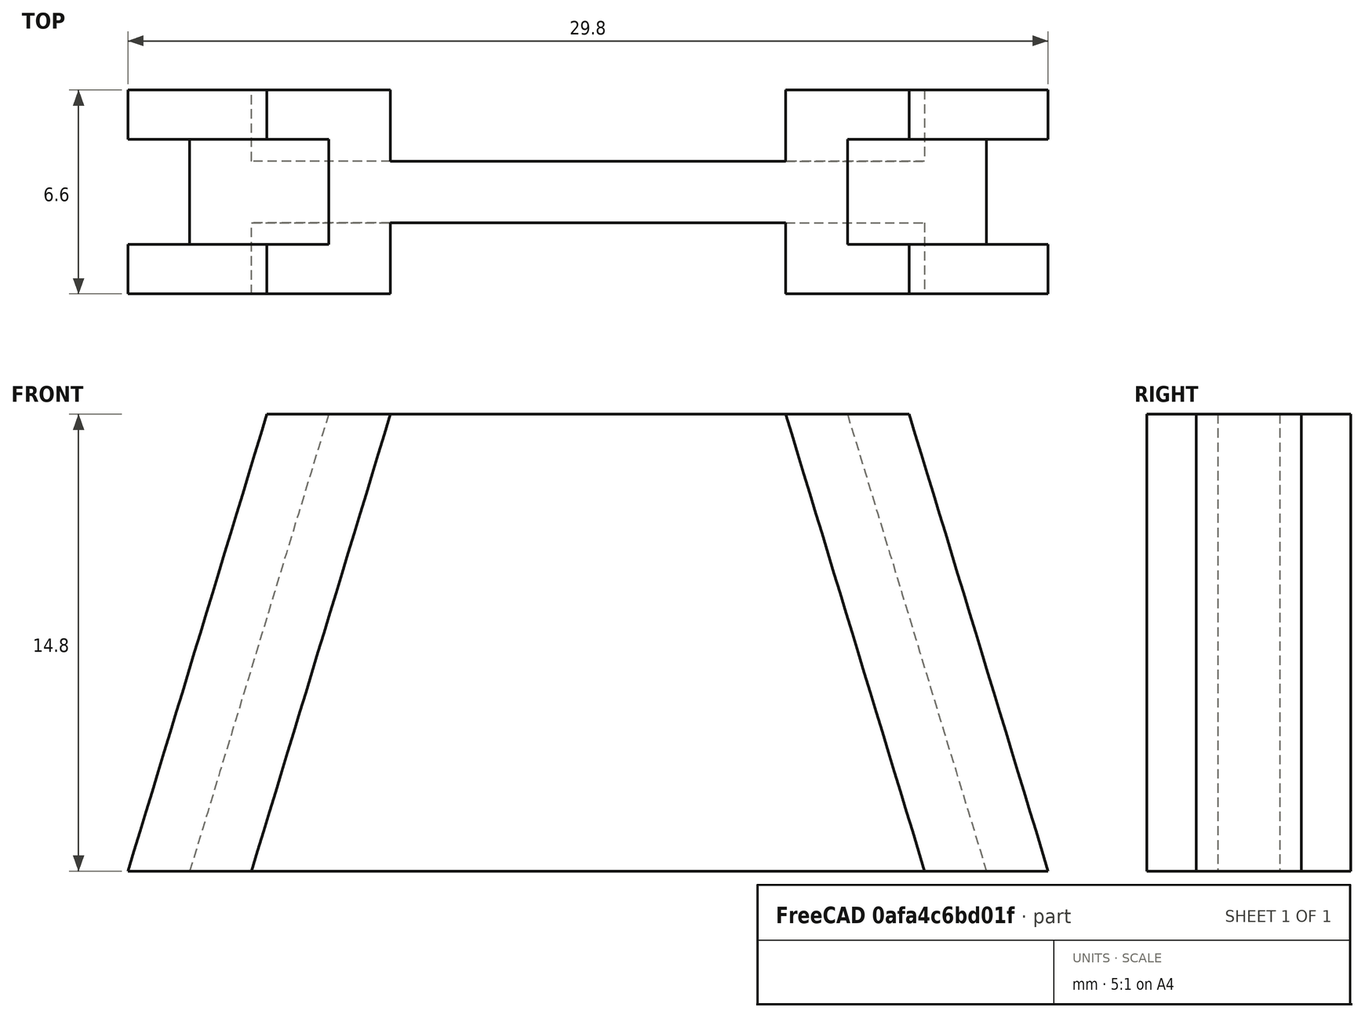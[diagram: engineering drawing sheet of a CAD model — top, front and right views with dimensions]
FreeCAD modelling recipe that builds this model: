
FCSTD DOCUMENT  (FreeCAD 0.18R4 (GitTag))
Label: smars_chassis_blank_v2
License: All rights reserved
LicenseURL: http://en.wikipedia.org/wiki/All_rights_reserved
objects: Sketcher::SketchObject×2, Part::Plane×1, PartDesign::AdditiveLoft×1, PartDesign::Body×1
note: 6 computed .brp shape members not serialized (recipe doc carries the construction recipe); baked Part::Feature solids carry a one-line shape summary decoded from their .brp

FEATURE [Part::Plane] Plane
  AttacherType = Attacher::AttachEngine3D
  Length = 10
  Placement = pos=(0,0,12.5) rot=(0,0,1;0rad)
  Width = 10
FEATURE [Sketcher::SketchObject] Sketch001  label="top"
  Support = -> [Plane]
  sketch-geometry (20):
    g0: LineSegment StartX=-14.9 StartY=-3.3 StartZ=0 EndX=-10.9 EndY=-3.3 EndZ=0
    g1: LineSegment StartX=-10.9 StartY=-3.3 StartZ=0 EndX=-10.9 EndY=-1 EndZ=0
    g2: LineSegment StartX=-10.9 StartY=-1 StartZ=0 EndX=10.9 EndY=-1 EndZ=0
    g3: LineSegment StartX=10.9 StartY=-1 StartZ=0 EndX=10.9 EndY=-3.3 EndZ=0
    g4: LineSegment StartX=10.9 StartY=-3.3 StartZ=0 EndX=14.9 EndY=-3.3 EndZ=0
    g5: LineSegment StartX=14.9 StartY=-3.3 StartZ=0 EndX=14.9 EndY=-1.7 EndZ=0
    g6: LineSegment StartX=14.9 StartY=-1.7 StartZ=0 EndX=12.9 EndY=-1.7 EndZ=0
    g7: LineSegment StartX=12.9 StartY=-1.7 StartZ=0 EndX=12.9 EndY=1.7 EndZ=0
    g8: LineSegment StartX=12.9 StartY=1.7 StartZ=0 EndX=14.9 EndY=1.7 EndZ=0
    g9: LineSegment StartX=14.9 StartY=1.7 StartZ=0 EndX=14.9 EndY=3.3 EndZ=0
    g10: LineSegment StartX=14.9 StartY=3.3 StartZ=0 EndX=10.9 EndY=3.3 EndZ=0
    g11: LineSegment StartX=10.9 StartY=3.3 StartZ=0 EndX=10.9 EndY=1 EndZ=0
    g12: LineSegment StartX=10.9 StartY=1 StartZ=0 EndX=-10.9 EndY=1 EndZ=0
    g13: LineSegment StartX=-10.9 StartY=1 StartZ=0 EndX=-10.9 EndY=3.3 EndZ=0
    g14: LineSegment StartX=-10.9 StartY=3.3 StartZ=0 EndX=-14.9 EndY=3.3 EndZ=0
    g15: LineSegment StartX=-14.9 StartY=3.3 StartZ=0 EndX=-14.9 EndY=1.7 EndZ=0
    g16: LineSegment StartX=-14.9 StartY=1.7 StartZ=0 EndX=-12.9 EndY=1.7 EndZ=0
    g17: LineSegment StartX=-12.9 StartY=1.7 StartZ=0 EndX=-12.9 EndY=-1.7 EndZ=0
    g18: LineSegment StartX=-12.9 StartY=-1.7 StartZ=0 EndX=-14.9 EndY=-1.7 EndZ=0
    g19: LineSegment StartX=-14.9 StartY=-1.7 StartZ=0 EndX=-14.9 EndY=-3.3 EndZ=0
  constraints (61):
    c: Coincident(g0,g1)
    c: Coincident(g1,g2)
    c: Coincident(g2,g3)
    c: Coincident(g3,g4)
    c: Coincident(g4,g5)
    c: Coincident(g5,g6)
    c: Coincident(g6,g7)
    c: Coincident(g7,g8)
    c: Coincident(g8,g9)
    c: Coincident(g9,g10)
    c: Coincident(g10,g11)
    c: Coincident(g11,g12)
    c: Coincident(g12,g13)
    c: Coincident(g13,g14)
    c: Coincident(g14,g15)
    c: Coincident(g15,g16)
    c: Coincident(g16,g17)
    c: Coincident(g17,g18)
    c: Coincident(g18,g19)
    c: Coincident(g19,g0)
    c: Horizontal(g14)
    c: Horizontal(g12)
    c: Horizontal(g10)
    c: Horizontal(g8)
    c: Horizontal(g6)
    c: Horizontal(g4)
    c: Horizontal(g16)
    c: Vertical(g15)
    c: Vertical(g19)
    c: Vertical(g17)
    c: Vertical(g13)
    c: Vertical(g3)
    c: Vertical(g11)
    c: Vertical(g9)
    c: Vertical(g7)
    c: Parallel(g16,g18)
    c: DistanceY(g15,g15) = 1.6
    c: Symmetric(g1,g2,g-2)
    c: Symmetric(g12,g1,g-1)
    c: Horizontal(g0)
    c: DistanceY(g1,g12) = 2
    c: DistanceY(g17,g17) = 3.4
    c: Equal(g15,g19)
    c: Equal(g19,g9)
    c: Equal(g9,g5)
    c: Equal(g17,g7)
    c: Equal(g13,g1)
    c: Equal(g1,g3)
    c: Equal(g3,g11)
    c: DistanceX(g14,g14) = 4
    c: DistanceX(g18,g18) = 2
    c: Equal(g14,g0)
    c: Equal(g0,g10)
    c: Equal(g10,g4)
    c: Equal(g15,g19)
    c: Equal(g19,g5)
    c: Equal(g5,g9)
    c: Equal(g18,g16)
    c: Equal(g16,g8)
    c: Equal(g8,g6)
    c: DistanceX(g16,g7) = 25.8
FEATURE [Sketcher::SketchObject] CopySketch002  label="bottom"
  Placement = pos=(0,0,14.8) rot=(0,0,1;0rad)
  sketch-geometry (20):
    g0: LineSegment StartX=-10.4 StartY=-3.3 StartZ=0 EndX=-6.39999 EndY=-3.3 EndZ=0
    g1: LineSegment StartX=-6.39999 StartY=-3.3 StartZ=0 EndX=-6.39999 EndY=-1 EndZ=0
    g2: LineSegment StartX=-6.39999 StartY=-1 StartZ=0 EndX=6.39999 EndY=-1 EndZ=0
    g3: LineSegment StartX=6.39999 StartY=-1 StartZ=0 EndX=6.39999 EndY=-3.3 EndZ=0
    g4: LineSegment StartX=6.39999 StartY=-3.3 StartZ=0 EndX=10.4 EndY=-3.3 EndZ=0
    g5: LineSegment StartX=10.4 StartY=-3.3 StartZ=0 EndX=10.4 EndY=-1.7 EndZ=0
    g6: LineSegment StartX=10.4 StartY=-1.7 StartZ=0 EndX=8.40001 EndY=-1.7 EndZ=0
    g7: LineSegment StartX=8.40001 StartY=-1.7 StartZ=0 EndX=8.40001 EndY=1.7 EndZ=0
    g8: LineSegment StartX=8.40001 StartY=1.7 StartZ=0 EndX=10.4 EndY=1.7 EndZ=0
    g9: LineSegment StartX=10.4 StartY=1.7 StartZ=0 EndX=10.4 EndY=3.3 EndZ=0
    g10: LineSegment StartX=10.4 StartY=3.3 StartZ=0 EndX=6.40001 EndY=3.3 EndZ=0
    g11: LineSegment StartX=6.40001 StartY=3.3 StartZ=0 EndX=6.40001 EndY=1 EndZ=0
    g12: LineSegment StartX=6.40001 StartY=1 StartZ=0 EndX=-6.39999 EndY=1 EndZ=0
    g13: LineSegment StartX=-6.39999 StartY=1 StartZ=0 EndX=-6.39999 EndY=3.3 EndZ=0
    g14: LineSegment StartX=-6.39999 StartY=3.3 StartZ=0 EndX=-10.4 EndY=3.3 EndZ=0
    g15: LineSegment StartX=-10.4 StartY=3.3 StartZ=0 EndX=-10.4 EndY=1.7 EndZ=0
    g16: LineSegment StartX=-10.4 StartY=1.7 StartZ=0 EndX=-8.39999 EndY=1.7 EndZ=0
    g17: LineSegment StartX=-8.39999 StartY=1.7 StartZ=0 EndX=-8.39999 EndY=-1.7 EndZ=0
    g18: LineSegment StartX=-8.39999 StartY=-1.7 StartZ=0 EndX=-10.4 EndY=-1.7 EndZ=0
    g19: LineSegment StartX=-10.4 StartY=-1.7 StartZ=0 EndX=-10.4 EndY=-3.3 EndZ=0
  constraints (61):
    c: Coincident(g0,g1)
    c: Coincident(g1,g2)
    c: Coincident(g2,g3)
    c: Coincident(g3,g4)
    c: Coincident(g4,g5)
    c: Coincident(g5,g6)
    c: Coincident(g6,g7)
    c: Coincident(g7,g8)
    c: Coincident(g8,g9)
    c: Coincident(g9,g10)
    c: Coincident(g10,g11)
    c: Coincident(g11,g12)
    c: Coincident(g12,g13)
    c: Coincident(g13,g14)
    c: Coincident(g14,g15)
    c: Coincident(g15,g16)
    c: Coincident(g16,g17)
    c: Coincident(g17,g18)
    c: Coincident(g18,g19)
    c: Coincident(g19,g0)
    c: Horizontal(g14)
    c: Horizontal(g12)
    c: Horizontal(g10)
    c: Horizontal(g8)
    c: Horizontal(g6)
    c: Horizontal(g4)
    c: Horizontal(g16)
    c: Vertical(g15)
    c: Vertical(g19)
    c: Vertical(g17)
    c: Vertical(g13)
    c: Vertical(g3)
    c: Vertical(g11)
    c: Vertical(g9)
    c: Vertical(g7)
    c: Parallel(g16,g18)
    c: DistanceY(g15,g15) = 1.6
    c: Symmetric(g1,g2,g-2)
    c: Symmetric(g12,g1,g-1)
    c: DistanceY(g1,g12) = 2
    c: DistanceY(g17,g17) = 3.4
    c: Equal(g15,g19)
    c: Equal(g19,g9)
    c: Equal(g9,g5)
    c: Equal(g17,g7)
    c: Equal(g13,g1)
    c: Equal(g1,g3)
    c: Equal(g3,g11)
    c: DistanceX(g14,g14) = 4
    c: DistanceX(g18,g18) = 2
    c: Equal(g14,g0)
    c: Equal(g0,g10)
    c: Equal(g10,g4)
    c: Equal(g15,g19)
    c: Equal(g19,g5)
    c: Equal(g5,g9)
    c: Equal(g18,g16)
    c: Equal(g16,g8)
    c: Equal(g8,g6)
    c: DistanceX(g16,g7) = 16.8
    c: Horizontal(g0)
FEATURE [PartDesign::AdditiveLoft] AdditiveLoft
  Closed = false
  Placement = pos=(0,0,14.8) rot=(0,0,1;0rad)
  Profile = -> CopySketch002
  Ruled = false
  Sections = -> [Sketch001]
FEATURE [PartDesign::Body] Body  label="Blank"
  Group = -> [AdditiveLoft]
  Origin = -> Origin
  Tip = -> AdditiveLoft
